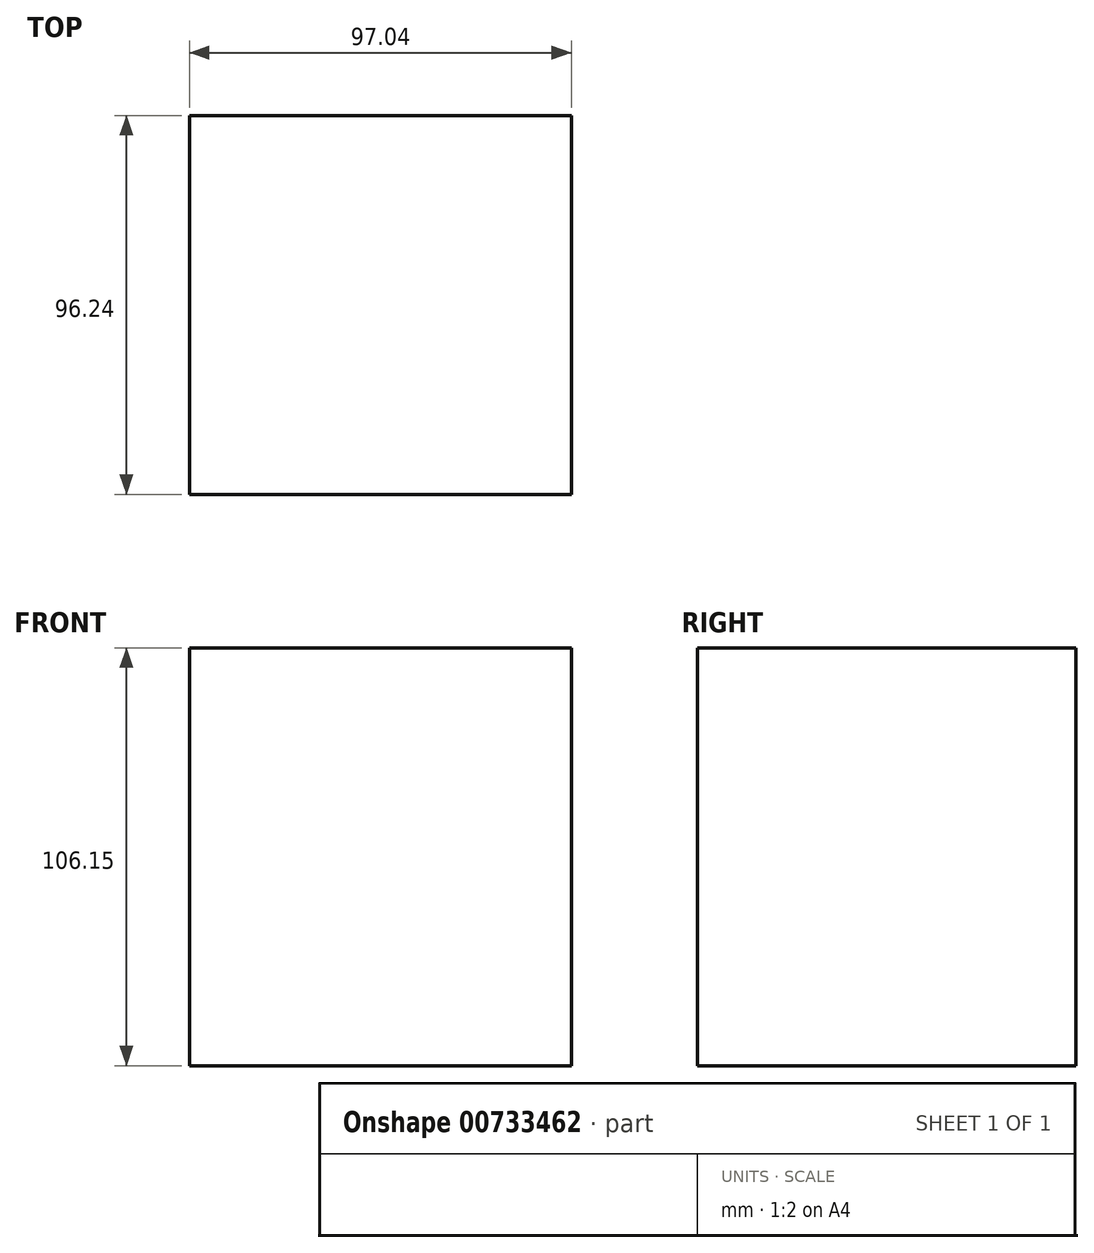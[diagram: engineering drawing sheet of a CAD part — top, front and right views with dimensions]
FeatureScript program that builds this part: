
annotation { "Feature Type Name" : "Feature", "Feature Type Description" : "" }
export const myFeature = defineFeature(function(context is Context, id is Id, definition is map)
    precondition{}
    {
        {
            var Q0;
            Q0=qCreatedBy(makeId("Front.planeOp"),FACE);
            var sketch = newSketch(context, id + "F0", { "sketchPlane" : qUnion([Q0])});
            skLineSegment(sketch, "E0.bottom", {"start": v(-46.31, 56.2) * mm, "end": v(50.73, 56.2) * mm});
            skLineSegment(sketch, "E0.top", {"start": v(-46.31, -49.95) * mm, "end": v(50.73, -49.95) * mm});
            skLineSegment(sketch, "E0.left", {"start": v(-46.31, 56.2) * mm, "end": v(-46.31, -49.95) * mm});
            skLineSegment(sketch, "E0.right", {"start": v(50.73, 56.2) * mm, "end": v(50.73, -49.95) * mm});
            skSolve(sketch);
        }
        {
            var Q0;
            Q0=makeQuery(id+"F0.imprint","IMPRINT",FACE,{"disambiguationData":[TD([[makeQuery(id+"F0.imprint","IMPRINT",EDGE,{"derivedFrom":sQuery(id+"F0.wireOp",EDGE,"E0.bottom")}),-1.0]])]});
            var sketch = newSketch(context, id + "F1", { "sketchPlane" : qUnion([Q0])});
            skSolve(sketch);
        }
        {
            var Q0;
            Q0=makeQuery(id+"F1.imprint","IMPRINT",FACE,{"disambiguationData":[TD([[makeQuery(id+"F1.imprint","IMPRINT",EDGE,{"derivedFrom":makeQuery(id+"F0.imprint","IMPRINT",EDGE,{"derivedFrom":sQuery(id+"F0.wireOp",EDGE,"E0.bottom")})}),-1.0]])]});
            extrude(context, id + "F2", {"entities" : qUnion([Q0]), "depth" : 25.4 * mm, "offsetDistance" : 25.4 * mm});
        }
        {
            var Q0;
            Q0=makeQuery(id+"F2.opExtrude","CAP_FACE",FACE,{"disambiguationData":[OSD([sQuery(id+"F0.wireOp",EDGE,"E0.bottom"),sQuery(id+"F0.wireOp",EDGE,"E0.top"),sQuery(id+"F0.wireOp",EDGE,"E0.left"),sQuery(id+"F0.wireOp",EDGE,"E0.right")])],"isStart":false});
            extrude(context, id + "F3", {"entities" : qUnion([Q0]), "operationType" : NewBodyOperationType.ADD, "depth" : 70.84 * mm, "offsetDistance" : 25.4 * mm});
        }
    });
